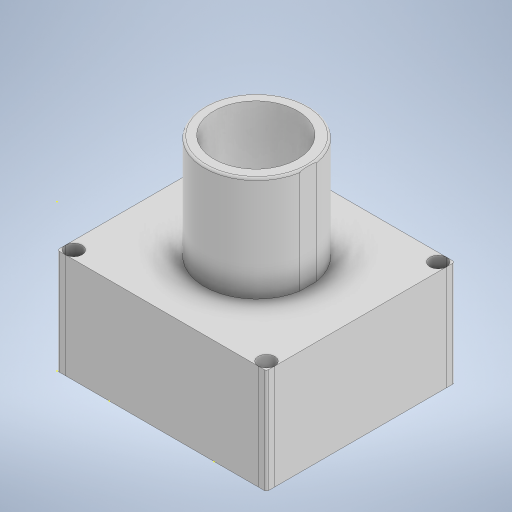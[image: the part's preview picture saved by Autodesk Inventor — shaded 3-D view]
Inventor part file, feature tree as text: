
AUTODESK INVENTOR PART (.ipt)
format: ipt  version: 2024 (Build 280153000, 153)  size: 288,256 bytes
history: native  units: in
note: dims shown in document units (in); Inventor stores cm internally (conversion verified against a paired STEP export)
features: sketch x8, extrude x4, fillet x2
ambient origin geometry x8: Origin, YZ Plane, XZ Plane, XY Plane, X Axis, Y Axis, Z Axis, Center Point
bodies: Solid1 (feature_tree)
feature tree (14):
  extrude  "Extrusion1"  Depth=19.685in
  fillet  "Fillet1"  Radius=3.1496in
  sketch  "Sketch2"  dims[d3=3.1496in d4=39.3701in]
  extrude  "Extrusion2"  Depth=39.3701in
  sketch  "Sketch4"  dims[d19=19.685in d20=0.0in d21=0.3937in]
  extrude  "Extrusion3"  Depth=0.3937in
  fillet  "Fillet2"  Radius=11.811in
  sketch  "Sketch6"  dims[d11=0.0344in]
  extrude  "Extrusion4"  Depth=0.3937in
  sketch  "Sketch8"  dims[d13=0.0in]
  sketch  "Sketch1"  dims[d0=39.3701in d1=19.685in d2=3.1496in]
  sketch  "Sketch3"  dims[d8=35.4331in d9=0.0in d10=0.3937in d14=11.811in d15=0.0in]
  sketch  "Sketch5"  dims[d30=19.685in d31=0.0in]
  sketch  "Sketch7"  dims[d12=0.0in]
